# Revit family: AVAD_Horizontal_Ceiling_Mount
name_source: partatom
category: Mechanical Equipment
units: mm (PartAtom-declared; Revit-internal decimal feet)

## family parameters
Always vertical = Yes
Cut with Voids When Loaded = No
Part Type = Normal
Room Calculation Point = No
Round Connector Dimension = Use Radius
Shared = No
Work Plane-Based = No

## types (8) — shared parameters
30 = 30.00°
60 = 60.00°
Four = 0' - 4"
Manufacturer = Loren Cook Company
Model = AVAD
ONE EIGTH = 0' - 0 1/8"
One = 0' - 1"
Oneandahalf = 0' - 1 1/2"
Three = 0' - 3"
Twentyfour = 2' - 0"
Two = 0' - 2"
Type Comments = Adjustable Pitch Vane Axial Horizontal Ceiling Mount Direct Drive Arrangement 4
URL = www.lorencook.com
ZERO = 0' - 0"
Zero = 0' - 0"

## per-type parameters (varying)
- 35_AVAD_HOR_CEILING: A=2' - 11 1/2"; AHalf=1' - 5 3/4"; AThrid=1' - 2 3/16"; Aa=1' - 5 7/8"; B=3' - 3 7/8"; BHalf=1' - 7 15/16"; C=3' - 2"; CHAlf=1' - 7"; E=2' - 6"; EHalf=1' - 3"; ELessTwo=2' - 4"; Ea=-1' - 3"; Eb=-1' - 2 7/8"; Ec=1' - 2 7/8"; F=0' - 0 9/16"; FHalf=0' - 0 9/32"; G=12' - 0"; H=1' - 9 1/8"; HHalf=0' - 10 9/16"; Ha=0' - 8 11/16"; J=0' - 4 7/16"; Ja=0' - 2 3/8"; K=3' - 3 5/8"; Khalf=1' - 7 13/16"; KminusA=0' - 4 1/8"; L=0' - 0 11/16"; LHalf=0' - 0 11/32"; La=-1' - 7"
- 39_AVAD_HOR_CEILING: A=3' - 3 3/8"; AHalf=1' - 7 11/16"; AThrid=1' - 3 3/4"; Aa=1' - 7 13/16"; B=3' - 7 15/16"; BHalf=1' - 9 31/32"; C=3' - 5 7/8"; CHAlf=1' - 8 15/16"; E=2' - 6"; EHalf=1' - 3"; ELessTwo=2' - 4"; Ea=-1' - 3"; Eb=-1' - 2 7/8"; Ec=1' - 2 7/8"; F=0' - 0 9/16"; FHalf=0' - 0 9/32"; G=12' - 0"; H=1' - 9 1/8"; HHalf=0' - 10 9/16"; Ha=0' - 8 23/32"; J=0' - 4 7/16"; Ja=0' - 2 5/16"; K=3' - 7 5/8"; Khalf=1' - 9 13/16"; KminusA=0' - 4 1/4"; L=0' - 0 11/16"; LHalf=0' - 0 11/32"; La=-1' - 8 15/16"
- 44_AVAD_HOR_CEILING: A=3' - 8 1/8"; AHalf=1' - 10 1/16"; AThrid=1' - 5 21/32"; Aa=1' - 10 3/16"; B=4' - 1 5/8"; BHalf=2' - 0 13/16"; C=3' - 11 3/8"; CHAlf=1' - 11 11/16"; E=2' - 10"; EHalf=1' - 5"; ELessTwo=2' - 8"; Ea=-1' - 5"; Eb=-1' - 4 7/8"; Ec=1' - 4 7/8"; F=0' - 0 9/16"; FHalf=0' - 0 9/32"; G=12' - 0"; H=1' - 11 1/4"; HHalf=0' - 11 5/8"; Ha=0' - 10 9/32"; J=0' - 5 3/8"; Ja=0' - 2 3/4"; K=4' - 1 3/8"; Khalf=2' - 0 11/16"; KminusA=0' - 5 1/4"; L=0' - 0 13/16"; LHalf=0' - 0 13/32"; La=-1' - 11 11/16"
- 49_AVAD_HOR_CEILING: A=4' - 1 1/4"; AHalf=2' - 0 5/8"; AThrid=1' - 7 11/16"; Aa=2' - 0 3/4"; B=4' - 6 3/4"; BHalf=2' - 3 3/8"; C=4' - 4 1/2"; CHAlf=2' - 2 1/4"; E=2' - 10"; EHalf=1' - 5"; ELessTwo=2' - 8"; Ea=-1' - 5"; Eb=-1' - 4 7/8"; Ec=1' - 4 7/8"; F=0' - 0 9/16"; FHalf=0' - 0 9/32"; G=12' - 0"; H=1' - 11 1/4"; HHalf=0' - 11 5/8"; Ha=0' - 9 15/32"; J=0' - 5 3/8"; Ja=0' - 2 3/4"; K=4' - 6 1/2"; Khalf=2' - 3 1/4"; KminusA=0' - 5 1/4"; L=0' - 0 13/16"; LHalf=0' - 0 13/32"; La=-2' - 2 1/4"
- 57_AVAD_HOR_CEILING: A=4' - 9 1/8"; AHalf=2' - 4 9/16"; AThrid=1' - 10 27/32"; Aa=2' - 4 11/16"; B=5' - 2 5/8"; BHalf=2' - 7 5/16"; C=4' - 11 7/8"; CHAlf=2' - 5 15/16"; E=3' - 6"; EHalf=1' - 9"; ELessTwo=3' - 4"; Ea=-1' - 9"; Eb=-1' - 8 7/8"; Ec=1' - 8 7/8"; F=0' - 0 9/16"; FHalf=0' - 0 9/32"; G=12' - 0"; H=2' - 7 1/4"; HHalf=1' - 3 5/8"; Ha=0' - 8 1/32"; J=0' - 5 3/8"; Ja=0' - 2 3/4"; K=5' - 2 3/8"; Khalf=2' - 7 3/16"; KminusA=0' - 5 1/4"; L=0' - 0 13/16"; LHalf=0' - 0 13/32"; La=-2' - 5 15/16"
- 63_AVAD_HOR_CEILING: A=5' - 3"; AHalf=2' - 7 1/2"; AThrid=2' - 1 3/16"; Aa=2' - 7 5/8"; B=5' - 8 1/2"; BHalf=2' - 10 1/4"; C=5' - 6 1/4"; CHAlf=2' - 9 1/8"; E=3' - 6"; EHalf=1' - 9"; ELessTwo=3' - 4"; Ea=-1' - 9"; Eb=-1' - 8 7/8"; Ec=1' - 8 7/8"; F=0' - 0 11/16"; FHalf=0' - 0 11/32"; G=16' - 0"; H=2' - 5"; HHalf=1' - 2 1/2"; Ha=0' - 7 5/8"; J=0' - 6 1/2"; Ja=0' - 3 3/8"; K=5' - 9 1/4"; Khalf=2' - 10 5/8"; KminusA=0' - 6 1/4"; L=0' - 1 1/16"; LHalf=0' - 0 17/32"; La=-2' - 9 1/8"
- 71_AVAD_HOR_CEILING: A=5' - 10 7/8"; AHalf=2' - 11 7/16"; AThrid=2' - 4 11/32"; Aa=2' - 11 9/16"; B=6' - 5 5/8"; BHalf=3' - 2 13/16"; C=6' - 3"; CHAlf=3' - 1 1/2"; E=4' - 6"; EHalf=2' - 3"; ELessTwo=4' - 4"; Ea=-2' - 3"; Eb=-2' - 2 7/8"; Ec=2' - 2 7/8"; F=0' - 0 11/16"; FHalf=0' - 0 11/32"; G=16' - 0"; H=3' - 5"; HHalf=1' - 8 1/2"; Ha=1' - 2 13/32"; J=0' - 6 1/2"; Ja=0' - 3 1/4"; K=6' - 5 3/8"; Khalf=3' - 2 11/16"; KminusA=0' - 6 1/2"; L=0' - 1 1/16"; LHalf=0' - 0 17/32"; La=-3' - 1 1/2"
- 79_AVAD_HOR_CEILING: A=6' - 6 3/4"; AHalf=3' - 3 3/8"; AThrid=2' - 7 1/2"; Aa=3' - 3 1/2"; B=7' - 1 9/16"; BHalf=3' - 6 25/32"; C=6' - 10 7/8"; CHAlf=3' - 5 7/16"; E=4' - 6"; EHalf=2' - 3"; ELessTwo=4' - 4"; Ea=-2' - 3"; Eb=-2' - 2 7/8"; Ec=2' - 2 7/8"; F=0' - 0 11/16"; FHalf=0' - 0 11/32"; G=16' - 0"; H=3' - 5"; HHalf=1' - 8 1/2"; Ha=1' - 1 15/16"; J=0' - 6 1/2"; Ja=0' - 3 1/4"; K=7' - 1 1/4"; Khalf=3' - 6 5/8"; KminusA=0' - 6 1/2"; L=0' - 1 1/16"; LHalf=0' - 0 17/32"; La=-3' - 5 7/16"

## geometry (parser evidence)
native form markers: Sweep x2
no freeform markers — native parametric forms only
